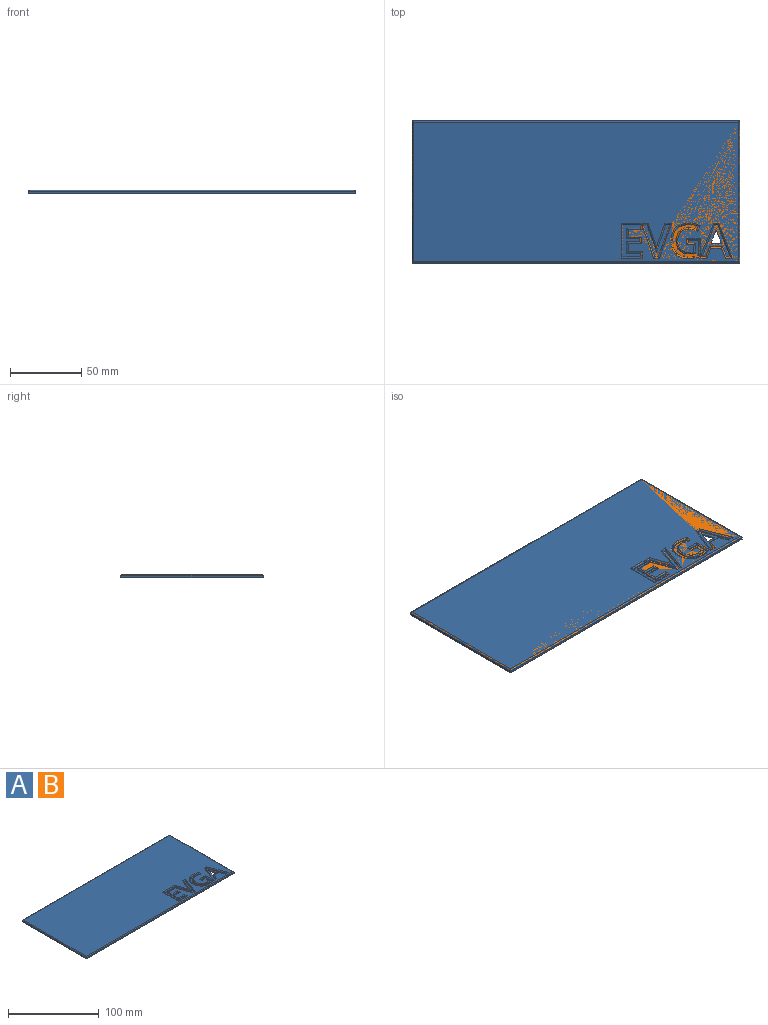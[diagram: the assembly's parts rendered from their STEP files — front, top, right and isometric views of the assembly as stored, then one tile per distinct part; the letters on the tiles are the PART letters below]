
ASSEMBLY  parts=2 mates=1
PART A: 116 faces, bbox 230x100x2.5 mm
  f0: plane 22.39x8.77mm, normal (-0.93,-0.36,0), area 12mm2, adj f1,f52,f63,f68
  f1: plane 2.68x0.5mm, normal (0,1,0), area 1.3mm2, adj f0,f2,f63,f66
  f2: plane 7.09x2.78mm, normal (0.93,0.36,0), area 3.8mm2, adj f1,f3,f63,f64
  f3: plane 8.94x0.5mm, normal (0,1,0), area 4.5mm2, adj f2,f4,f63,f65
  f4: plane 7.09x2.74mm, normal (-0.93,0.36,0), area 3.8mm2, adj f3,f5,f63,f67
  f5: plane 2.63x0.5mm, normal (0,1,0), area 1.3mm2, adj f4,f6,f63,f69
  f6: plane 22.39x8.82mm, normal (0.93,-0.37,0), area 12mm2, adj f5,f52,f63,f71
  f7: plane 4.98x0.5mm, normal (0,1,0), area 2.5mm2, adj f8,f48,f57,f90
  f8: plane 2.32x0.5mm, normal (1,0,0), area 1.2mm2, adj f7,f9,f57,f88
  f9: plane 7.58x0.5mm, normal (0,-1,0), area 3.8mm2, adj f8,f10,f57,f86
  f10: plane 10.85x0.5mm, normal (-1,0,0), area 5.4mm2, adj f9,f11,f57,f84
  f11: extruded ~3.6x0.86mm, area 1.9mm2, adj f10,f12,f57,f82
  f12: extruded ~4.24x0.5mm, area 2.1mm2, adj f11,f13,f57,f80
  f13: extruded ~7.88x3.01mm, area 4.3mm2, adj f12,f14,f57,f78
  f14: extruded ~8.44x2.82mm, area 4.6mm2, adj f13,f15,f57,f76
  f15: extruded ~6.1x1.4mm, area 3.2mm2, adj f14,f16,f57,f74
  f16: extruded ~4.02x4mm, area 2.9mm2, adj f15,f17,f57,f72
  f17: extruded ~6.14x1.38mm, area 3.2mm2, adj f16,f18,f57,f73
  f18: extruded ~6.65x1.31mm, area 3.4mm2, adj f17,f19,f57,f75
  f19: plane 2.29x1.01mm, normal (-0.92,0.4,0), area 1.3mm2, adj f18,f20,f57,f77
  f20: extruded ~5.81x1.28mm, area 3mm2, adj f19,f21,f57,f79
  f21: extruded ~6.36x2.42mm, area 3.5mm2, adj f20,f22,f57,f81
  f22: extruded ~6.73x2.29mm, area 3.6mm2, adj f21,f23,f57,f83
  f23: extruded ~6.85x2.2mm, area 3.7mm2, adj f22,f24,f57,f85
  f24: extruded ~6.47x2.33mm, area 3.5mm2, adj f23,f25,f57,f87
  f25: extruded ~4.53x0.54mm, area 2.3mm2, adj f24,f48,f57,f89
  f26: extruded ~4.93x1.44mm, area 2.6mm2, adj f27,f49,f56,f110
  f27: plane 14.34x5.1mm, normal (0.94,-0.33,0), area 7.6mm2, adj f26,f28,f56,f108
  f28: plane 2.79x0.5mm, normal (0,-1,0), area 1.4mm2, adj f27,f29,f56,f107
  f29: plane 22.3x8.03mm, normal (-0.94,0.34,0), area 11.9mm2, adj f28,f30,f56,f105
  f30: plane 2.56x0.5mm, normal (0,1,0), area 1.3mm2, adj f29,f31,f56,f102
  f31: plane 22.3x8mm, normal (0.94,0.34,0), area 11.8mm2, adj f30,f32,f56,f106
  f32: plane 2.75x0.5mm, normal (0,-1,0), area 1.4mm2, adj f31,f33,f56,f104
  f33: plane 14.43x5.13mm, normal (-0.94,-0.33,0), area 7.7mm2, adj f32,f49,f56,f109
  f34: plane 9.84x0.5mm, normal (0,-1,0), area 4.9mm2, adj f35,f50,f55,f95
  f35: plane 2.32x0.5mm, normal (-1,0,0), area 1.2mm2, adj f34,f36,f55,f97
  f36: plane 12.43x0.5mm, normal (0,1,0), area 6.2mm2, adj f35,f37,f55,f99
  f37: plane 22.3x0.5mm, normal (1,0,0), area 11.2mm2, adj f36,f38,f55,f101
  f38: plane 12.43x0.5mm, normal (0,-1,0), area 6.2mm2, adj f37,f39,f55,f104
  f39: plane 2.3x0.5mm, normal (-1,0,0), area 1.2mm2, adj f38,f40,f55,f103
  f40: plane 9.84x0.5mm, normal (0,1,0), area 4.9mm2, adj f39,f41,f55,f100
  f41: plane 7.18x0.5mm, normal (-1,0,0), area 3.6mm2, adj f40,f42,f55,f98
  f42: plane 9.24x0.5mm, normal (0,-1,0), area 4.6mm2, adj f41,f43,f55,f96
  f43: plane 2.29x0.5mm, normal (-1,0,0), area 1.1mm2, adj f42,f44,f55,f94
  f44: plane 9.24x0.5mm, normal (0,1,0), area 4.6mm2, adj f43,f50,f55,f92
  f45: plane 230x1.5mm, normal (0,1,0), area 345mm2, adj f46,f51,f54,f113
  f46: plane 100x1.5mm, normal (-1,0,0), area 150mm2, adj f45,f47,f54,f112
  f47: plane 230x1.5mm, normal (0,-1,0), area 345mm2, adj f46,f51,f54,f114
  f48: plane 6.86x0.5mm, normal (1,0,0), area 3.4mm2, adj f7,f25,f57,f91
  f49: extruded ~4.84x1.4mm, area 2.5mm2, adj f26,f33,f56,f111
  f50: plane 8.21x0.5mm, normal (-1,0,0), area 4.1mm2, adj f34,f44,f55,f93
  f51: plane 100x1.5mm, normal (1,0,0), area 150mm2, adj f45,f47,f54,f115
  f52: plane 2.18x0.5mm, normal (0,-1,0), area 1.1mm2, adj f0,f6,f63,f70
  f53: plane 228x98mm, normal (0,0,1), area 21368.3mm2, adj f64,f65,f66,f67,f68,f69,f70,f71
  f54: plane 230x100mm, normal (0,0,-1), area 22965.2mm2, adj f45,f46,f47,f51,f58,f59,f60,f61
  f55: plane 22.3x12.43mm, normal (0,0,1), area 124.4mm2, adj f34,f35,f36,f37,f38,f39,f40,f41
  f56: plane 22.3x18.59mm, normal (0,0,1), area 115.2mm2, adj f26,f27,f28,f29,f30,f31,f32,f33
  f57: plane 22.93x18.55mm, normal (0,0,1), area 150.6mm2, adj f7,f8,f9,f10,f11,f12,f13,f14
  f58: plane 7.21x1mm, normal (0,1,0), area 7.2mm2, adj f54,f59,f62,f63
  f59: plane 6.91x2.62mm, normal (0.94,-0.35,0), area 7.4mm2, adj f54,f58,f60,f63
  f60: extruded ~3.22x1mm, area 3.4mm2, adj f54,f59,f61,f63
  f61: extruded ~3.22x1.03mm, area 3.4mm2, adj f54,f60,f62,f63
  f62: plane 6.91x2.6mm, normal (-0.94,-0.35,0), area 7.4mm2, adj f54,f58,f61,f63
  f63: plane 22.39x19.77mm, normal (0,0,1), area 128mm2, adj f0,f1,f2,f3,f4,f5,f6,f52
  f64: cylinder r=1mm len=8.09mm, axis (0.36,-0.93,0), area 12mm2, adj f2,f53,f65,f66
  f65: cylinder r=1mm len=8.94mm, axis (1,0,0), area 13mm2, adj f3,f53,f64,f67
  f66: cylinder r=1mm len=4.83mm, axis (1,0,0), area 5.9mm2, adj f1,f53,f64,f68
  f67: cylinder r=1mm len=8.09mm, axis (0.36,0.93,0), area 11.9mm2, adj f4,f53,f65,f69
  f68: cylinder r=1mm len=24.76mm, axis (-0.36,0.93,0), area 39.5mm2, adj f0,f53,f66,f70
  f69: cylinder r=1mm len=4.78mm, axis (1,0,0), area 5.8mm2, adj f5,f53,f67,f71
  f70: cylinder r=1mm len=3.55mm, axis (-1,0,0), area 4.5mm2, adj f52,f53,f68,f71
  f71: cylinder r=1mm len=24.76mm, axis (-0.37,-0.93,0), area 39.5mm2, adj f6,f53,f69,f70
  f72: bspline ~6.39x6.36mm, area 9.4mm2, adj f16,f53,f73,f74
  f73: bspline ~8.99x2.97mm, area 10.3mm2, adj f17,f53,f72,f75
  f74: bspline ~8.92x2.99mm, area 10.2mm2, adj f15,f53,f72,f76
  f75: bspline ~13.6x4.42mm, area 11.7mm2, adj f18,f53,f73,f77
  f76: bspline ~12.95x4.11mm, area 14.8mm2, adj f14,f53,f74,f78
  f77: cylinder r=1mm len=4.52mm, axis (0.4,0.92,0), area 5.5mm2, adj f19,f53,f75,f79
  f78: bspline ~10.36x5.09mm, area 14.1mm2, adj f13,f53,f76,f80
  f79: bspline ~7.24x2.64mm, area 10mm2, adj f20,f53,f77,f81
  f80: bspline ~6.05x1.42mm, area 6.8mm2, adj f12,f53,f78,f82
  f81: bspline ~9.49x3.96mm, area 10.5mm2, adj f21,f53,f79,f83
  f82: bspline ~7.18x2.76mm, area 6.5mm2, adj f11,f53,f80,f84
  f83: bspline ~10.41x3.94mm, area 11mm2, adj f22,f53,f81,f85
  f84: cylinder r=1mm len=12.58mm, axis (0,1,0), area 18.4mm2, adj f10,f53,f82,f86
  f85: bspline ~10.65x3.89mm, area 11.1mm2, adj f23,f53,f83,f87
  f86: cylinder r=1mm len=9.58mm, axis (-1,0,0), area 13.5mm2, adj f9,f53,f84,f88
  f87: bspline ~7.91x3.89mm, area 10.7mm2, adj f24,f53,f85,f89
  f88: cylinder r=1mm len=4.32mm, axis (0,-1,0), area 5.2mm2, adj f8,f53,f86,f90
  f89: bspline ~6.08x1.64mm, area 6.4mm2, adj f25,f53,f87,f91
  f90: cylinder r=1mm len=5.98mm, axis (1,0,0), area 7.8mm2, adj f7,f53,f88,f91
  f91: cylinder r=1mm len=6.86mm, axis (0,-1,0), area 9.4mm2, adj f48,f53,f89,f90
  f92: cylinder r=1mm len=10.24mm, axis (1,0,0), area 14.5mm2, adj f44,f53,f93,f94
  f93: cylinder r=1mm len=8.21mm, axis (0,1,0), area 11.3mm2, adj f50,f53,f92,f95
  f94: cylinder r=1mm len=4.29mm, axis (0,1,0), area 5.2mm2, adj f43,f53,f92,f96
  f95: cylinder r=1mm len=10.84mm, axis (-1,0,0), area 15.5mm2, adj f34,f53,f93,f97
  f96: cylinder r=1mm len=10.24mm, axis (-1,0,0), area 14.5mm2, adj f42,f53,f94,f98
  f97: cylinder r=1mm len=4.32mm, axis (0,1,0), area 5.2mm2, adj f35,f53,f95,f99
  f98: cylinder r=1mm len=7.18mm, axis (0,1,0), area 9.7mm2, adj f41,f53,f96,f100
  f99: cylinder r=1mm len=14.43mm, axis (1,0,0), area 21.1mm2, adj f36,f53,f97,f101
  f100: cylinder r=1mm len=10.84mm, axis (1,0,0), area 15.5mm2, adj f40,f53,f98,f103
  f101: cylinder r=1mm len=24.3mm, axis (0,-1,0), area 36.6mm2, adj f37,f53,f99,f104
  f102: cylinder r=1mm len=3.97mm, axis (1,0,0), area 5.1mm2, adj f30,f53,f105,f106
  f103: cylinder r=1mm len=4.08mm, axis (0,1,0), area 5mm2, adj f39,f53,f100,f104,f106
  f104: cylinder r=1mm len=18.76mm, axis (-1,0,0), area 26.9mm2, adj f32,f38,f53,f101,f103,f106,f109
  f105: cylinder r=1mm len=24.64mm, axis (0.34,0.94,0), area 38.9mm2, adj f29,f53,f102,f107
  f106: cylinder r=1mm len=24.34mm, axis (0.34,-0.94,0), area 38.6mm2, adj f31,f53,f102,f103,f104
  f107: cylinder r=1mm len=4.92mm, axis (-1,0,0), area 6mm2, adj f28,f53,f105,f108
  f108: cylinder r=1mm len=15.34mm, axis (-0.33,-0.94,0), area 24.5mm2, adj f27,f53,f107,f110
  f109: cylinder r=1mm len=15.43mm, axis (-0.33,0.94,0), area 24.6mm2, adj f33,f53,f104,f111
  f110: bspline ~6.48x2.72mm, area 5.2mm2, adj f26,f53,f108,f111
  f111: bspline ~6.56x2.72mm, area 5.1mm2, adj f49,f53,f109,f110
  f112: cylinder r=1mm len=100mm, axis (0,1,0), area 155.5mm2, adj f46,f53,f113,f114
  f113: cylinder r=1mm len=230mm, axis (1,0,0), area 359.7mm2, adj f45,f53,f112,f115
  f114: cylinder r=1mm len=230mm, axis (-1,0,0), area 359.7mm2, adj f47,f53,f112,f115
  f115: cylinder r=1mm len=100mm, axis (0,-1,0), area 155.5mm2, adj f51,f53,f113,f114
PART B: same geometry as A
PLACE A at identity
PLACE B at identity
MATE planar A.f53 <-> B.f53  axis (0,0,1) through (-5.99,1.58,2.5)mm
